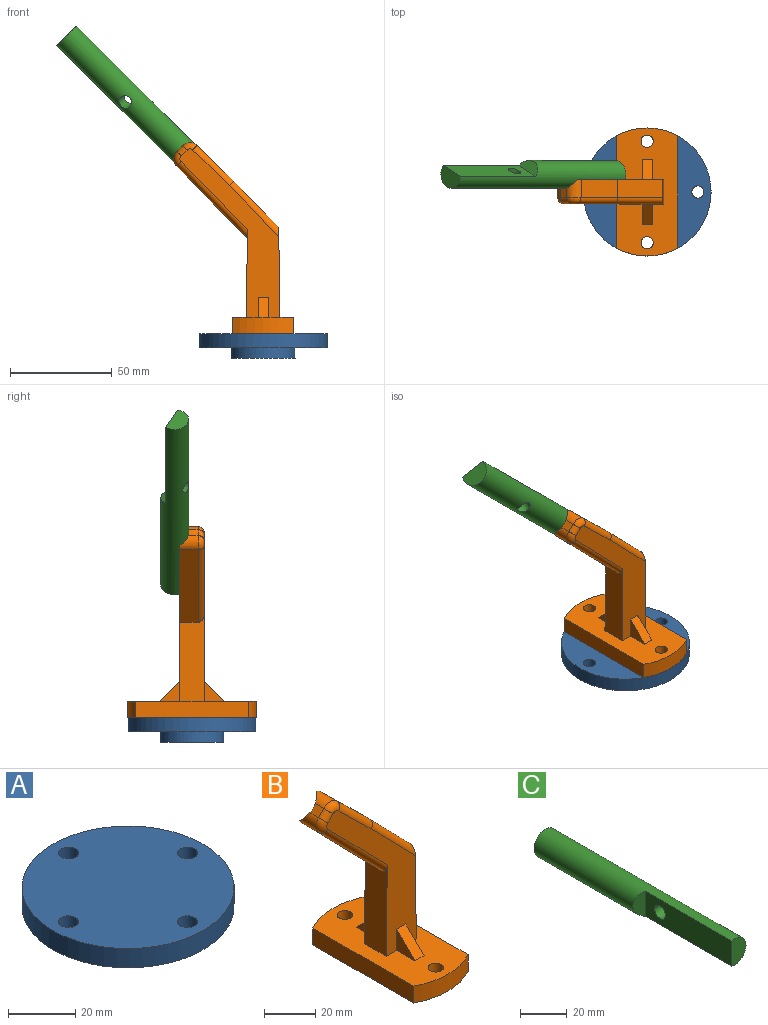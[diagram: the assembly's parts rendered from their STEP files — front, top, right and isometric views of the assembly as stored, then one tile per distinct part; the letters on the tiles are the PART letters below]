
ASSEMBLY  parts=3 mates=2
PART A: 9 faces, bbox 63x63x12 mm
  f0: plane 63x63mm, normal (0,0,-1), area 2224.8mm2, adj f2,f3,f4,f5,f6,f7
  f1: plane 63x63mm, normal (0,0,1), area 3004.1mm2, adj f2,f3,f4,f5,f6
  f2: cylinder r=31.5mm len=63mm, axis (0,0,1), area 1385.4mm2, adj f0,f1
  f3: cylinder r=3mm len=7mm, axis (0,0,1), area 131.9mm2, adj f0,f1
  f4: cylinder r=3mm len=7mm, axis (0,0,1), area 131.9mm2, adj f0,f1
  f5: cylinder r=3mm len=7mm, axis (0,0,1), area 131.9mm2, adj f0,f1
  f6: cylinder r=3mm len=7mm, axis (0,0,1), area 131.9mm2, adj f0,f1
  f7: cylinder r=15.75mm len=31.5mm, axis (0,0,1), area 494.8mm2, adj f0,f8
  f8: plane 31.5x31.5mm, normal (0,0,-1), area 779.3mm2, adj f7
PART B: 32 faces, bbox 60.6x63x95.6 mm
  f0: plane 18.06x17.61mm, normal (0.7,0,0.72), area 227mm2, adj f4,f20,f23,f27
  f1: plane 43.14x12mm, normal (-1,0,0.01), area 469.6mm2, adj f2,f4,f5,f19,f28
  f2: plane 82.93x49.17mm, normal (0,-1,0), area 1086mm2, adj f1,f3,f5,f13,f14,f15,f26,f27
  f3: plane 44.18x12mm, normal (1,0,0.01), area 527.4mm2, adj f2,f4,f5,f23,f26
  f4: plane 85.67x51.92mm, normal (0,1,0), area 804.7mm2, adj f0,f1,f3,f5,f16,f17,f18,f19
  f5: plane 63x30mm, normal (0,0,1), area 1461.6mm2, adj f1,f2,f3,f4,f6,f7,f8,f9
  f6: plane 55.4x8mm, normal (1,0,0), area 443.2mm2, adj f5,f7,f11,f12
  f7: cylinder r=31.5mm len=30mm, axis (0,0,-1), area 250.1mm2, adj f5,f6,f8,f12
  f8: plane 55.4x8mm, normal (-1,0,0), area 443.2mm2, adj f5,f7,f11,f12
  f9: cylinder r=3mm len=8mm, axis (0,0,-1), area 150.8mm2, adj f5,f12
  f10: cylinder r=3mm len=8mm, axis (0,0,-1), area 150.8mm2, adj f5,f12
  f11: cylinder r=31.5mm len=30mm, axis (0,0,-1), area 250.1mm2, adj f5,f6,f8,f12
  f12: plane 63x30mm, normal (0,0,-1), area 1759.4mm2, adj f6,f7,f8,f9,f10,f11
  f13: plane 10x10mm, normal (-1,0,0), area 50mm2, adj f2,f5,f15
  f14: plane 10x10mm, normal (1,0,0), area 50mm2, adj f2,f5,f15
  f15: plane 10x10mm, normal (0,-0.71,0.71), area 70.7mm2, adj f2,f5,f13,f14
  f16: plane 10x10mm, normal (1,0,0), area 50mm2, adj f4,f5,f18
  f17: plane 10x10mm, normal (-1,0,0), area 50mm2, adj f4,f5,f18
  f18: plane 10x10mm, normal (0,0.71,0.71), area 70.7mm2, adj f4,f5,f16,f17
  f19: plane 35.63x34.76mm, normal (-0.72,0,-0.7), area 448mm2, adj f1,f4,f22,f28
  f20: cylinder r=5mm len=9mm, axis (0,-1,0), area 56.3mm2, adj f0,f4,f21,f25,f29
  f21: plane 4.81x2.92mm, normal (-0.71,0,0.71), area 19mm2, adj f20,f22,f25,f31
  f22: cylinder r=5mm len=9mm, axis (0,1,0), area 56.3mm2, adj f4,f19,f21,f25,f30
  f23: plane 22.72x22.16mm, normal (0.72,0,0.7), area 285.7mm2, adj f0,f3,f4,f26
  f24: plane 9.25x9.25mm, normal (-0.71,0,0.71), area 42.7mm2, adj f4,f25
  f25: cylinder r=7mm len=44.6mm, axis (-0.71,0,0.71), area 831.2mm2, adj f4,f20,f21,f22,f24
  f26: cylinder r=3mm len=27.07mm, axis (-0.7,0,0.72), area 154.9mm2, adj f2,f3,f23,f27
  f27: cylinder r=3mm len=20.15mm, axis (-0.72,0,0.7), area 118.8mm2, adj f0,f2,f26,f29
  f28: cylinder r=3mm len=37.72mm, axis (0.7,0,-0.72), area 229.4mm2, adj f1,f2,f19,f30
  f29: torus R=2mm, axis (0,-1,0), area 28.7mm2, adj f2,f20,f27,f31
  f30: torus R=2mm, axis (0,-1,0), area 28.7mm2, adj f2,f22,f28,f31
  f31: cylinder r=3mm len=5.04mm, axis (-0.71,0,-0.71), area 19.4mm2, adj f2,f21,f29,f30
PART C: 6 faces, bbox 13.7x115x13.7 mm
  f0: cylinder r=6.85mm len=115mm, axis (0,1,0), area 3952.5mm2, adj f1,f2,f3,f4,f5
  f1: plane 13.7x8.7mm, normal (0,-1,0), area 98.7mm2, adj f0,f4
  f2: plane 13.7x13.7mm, normal (0,1,0), area 147.4mm2, adj f0
  f3: plane 13.19x5mm, normal (-0.45,-0.89,0), area 54.4mm2, adj f0,f4
  f4: plane 52.5x13.19mm, normal (-1,0,0), area 658.3mm2, adj f0,f1,f3,f5
  f5: cylinder r=3.3mm len=8.7mm, axis (-1,0,0), area 171.8mm2, adj f0,f4
PLACE A t=(-16,-1.16,15.86)mm fixed
PLACE B t=(-16,-1.16,15.86)mm
PLACE C rot(axis=(-0.15,0.5,-0.85),109.5deg) t=(-73.74,7.34,123.6)mm
MATE fastened B.f7 <-> A.f2  axis (0,0,-1) through (-16,-1.16,15.86)mm
MATE cylindrical C.f0 <-> B.f25  axis (0.71,0,-0.71) through (-31.32,7.34,81.18)mm
